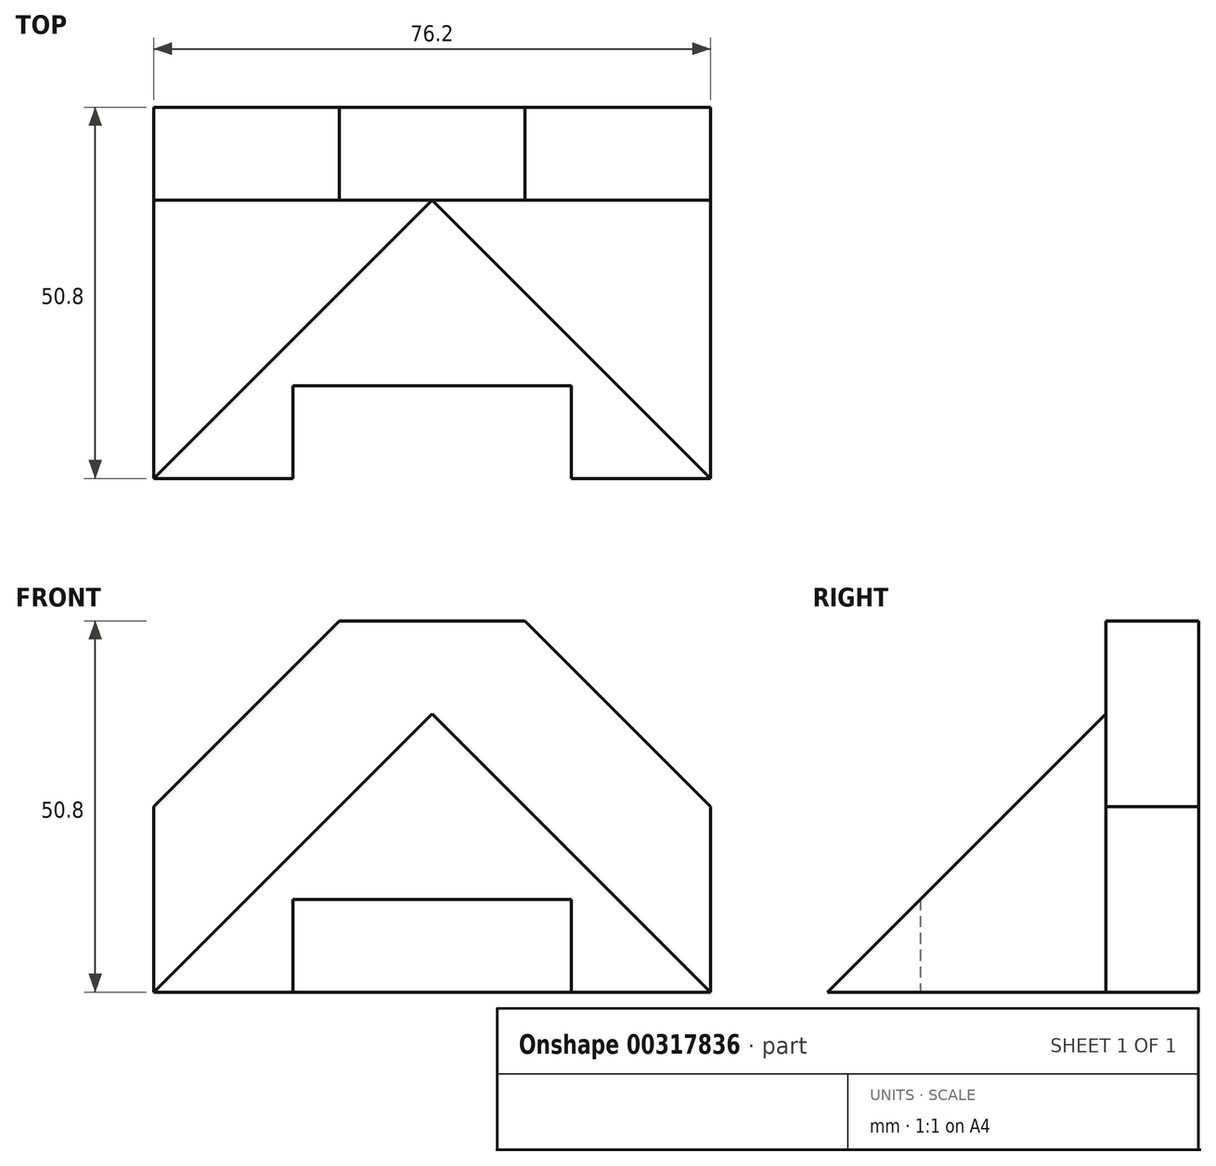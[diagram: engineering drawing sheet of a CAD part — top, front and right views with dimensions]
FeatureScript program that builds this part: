
annotation { "Feature Type Name" : "Feature", "Feature Type Description" : "" }
export const myFeature = defineFeature(function(context is Context, id is Id, definition is map)
    precondition{}
    {
        {
            var Q0;
            Q0=qCreatedBy(makeId("Top.planeOp"),FACE);
            var sketch = newSketch(context, id + "F0", { "sketchPlane" : qUnion([Q0])});
            skLineSegment(sketch, "E0", {"start": v(-38.1, 0) * mm, "end": v(38.1, 0) * mm});
            skLineSegment(sketch, "E1", {"start": v(38.1, 0) * mm, "end": v(38.1, 12.7) * mm});
            skLineSegment(sketch, "E2", {"start": v(38.1, 12.7) * mm, "end": v(-38.1, 12.7) * mm});
            skLineSegment(sketch, "E3", {"start": v(-38.1, 12.7) * mm, "end": v(-38.1, 0) * mm});
            skSolve(sketch);
        }
        {
            var Q0;
            Q0 = qSketchRegion(id + "F0", true);
            extrude(context, id + "F1", {"entities" : qUnion([Q0]), "depth" : 50.8 * mm});
        }
        {
            var Q0;
            Q0=makeQuery(id+"F1.opExtrude","SWEPT_FACE",FACE,{"disambiguationData":[OSD([sQuery(id+"F0.wireOp",EDGE,"E0")])]});
            var sketch = newSketch(context, id + "F2", { "sketchPlane" : qUnion([Q0])});
            skLineSegment(sketch, "E4", {"start": v(-38.1, 50.8) * mm, "end": v(-12.7, 50.8) * mm});
            skLineSegment(sketch, "E5", {"start": v(-12.7, 50.8) * mm, "end": v(-38.1, 25.4) * mm});
            skLineSegment(sketch, "E6", {"start": v(-38.1, 25.4) * mm, "end": v(-38.1, 50.8) * mm});
            skLineSegment(sketch, "E7", {"start": v(12.7, 50.8) * mm, "end": v(38.1, 50.8) * mm});
            skLineSegment(sketch, "E8", {"start": v(38.1, 50.8) * mm, "end": v(38.1, 25.4) * mm});
            skLineSegment(sketch, "E9", {"start": v(38.1, 25.4) * mm, "end": v(12.7, 50.8) * mm});
            skSolve(sketch);
        }
        {
            var Q0;
            Q0 = qSketchRegion(id + "F2", true);
            extrude(context, id + "F3", {"entities" : qUnion([Q0]), "operationType" : NewBodyOperationType.REMOVE, "endBound" : BoundingType.THROUGH_ALL, "oppositeDirection" : true, "depth" : 25.4 * mm});
        }
        {
            var Q0;
            Q0=makeQuery(id+"F1.opExtrude","SWEPT_FACE",FACE,{"disambiguationData":[OSD([sQuery(id+"F0.wireOp",EDGE,"E0")])]});
            var sketch = newSketch(context, id + "F4", { "sketchPlane" : qUnion([Q0])});
            skLineSegment(sketch, "E10", {"start": v(0, 38.1) * mm, "end": v(-38.1, 0) * mm});
            skLineSegment(sketch, "E11", {"start": v(-38.1, 0) * mm, "end": v(38.1, 0) * mm});
            skLineSegment(sketch, "E12", {"start": v(38.1, 0) * mm, "end": v(0, 38.1) * mm});
            skSolve(sketch);
        }
        {
            var Q0;
            Q0 = qSketchRegion(id + "F4", true);
            extrude(context, id + "F5", {"entities" : qUnion([Q0]), "operationType" : NewBodyOperationType.ADD, "depth" : 38.1 * mm});
        }
        {
            var Q0;
            Q0=qCreatedBy(makeId("Right.planeOp"),FACE);
            var sketch = newSketch(context, id + "F6", { "sketchPlane" : qUnion([Q0])});
            skLineSegment(sketch, "E13", {"start": v(0, 38.1) * mm, "end": v(-38.1, 0) * mm});
            skLineSegment(sketch, "E14", {"start": v(-38.1, 0) * mm, "end": v(-38.1, 38.1) * mm});
            skLineSegment(sketch, "E15", {"start": v(-38.1, 38.1) * mm, "end": v(0, 38.1) * mm});
            skSolve(sketch);
        }
        {
            var Q0;
            Q0 = qSketchRegion(id + "F6", true);
            extrude(context, id + "F7", {"entities" : qUnion([Q0]), "operationType" : NewBodyOperationType.REMOVE, "endBound" : BoundingType.THROUGH_ALL, "oppositeDirection" : true, "depth" : 25.4 * mm, "hasSecondDirection" : true, "secondDirectionBound" : SecondDirectionBoundingType.THROUGH_ALL, "secondDirectionOppositeDirection" : false, "secondDirectionDepth" : 47.5 * mm});
        }
        {
            var Q0;
            Q0=qCreatedBy(makeId("Top.planeOp"),FACE);
            var sketch = newSketch(context, id + "F8", { "sketchPlane" : qUnion([Q0])});
            skLineSegment(sketch, "E16.bottom", {"start": v(-19.05, -25.4) * mm, "end": v(19.05, -25.4) * mm});
            skLineSegment(sketch, "E16.top", {"start": v(-19.05, -38.1) * mm, "end": v(19.05, -38.1) * mm});
            skLineSegment(sketch, "E16.left", {"start": v(-19.05, -25.4) * mm, "end": v(-19.05, -38.1) * mm});
            skLineSegment(sketch, "E16.right", {"start": v(19.05, -25.4) * mm, "end": v(19.05, -38.1) * mm});
            skSolve(sketch);
        }
        {
            var Q0;
            Q0 = qSketchRegion(id + "F8", true);
            extrude(context, id + "F9", {"entities" : qUnion([Q0]), "operationType" : NewBodyOperationType.REMOVE, "endBound" : BoundingType.THROUGH_ALL, "depth" : 25.4 * mm});
        }
    });
